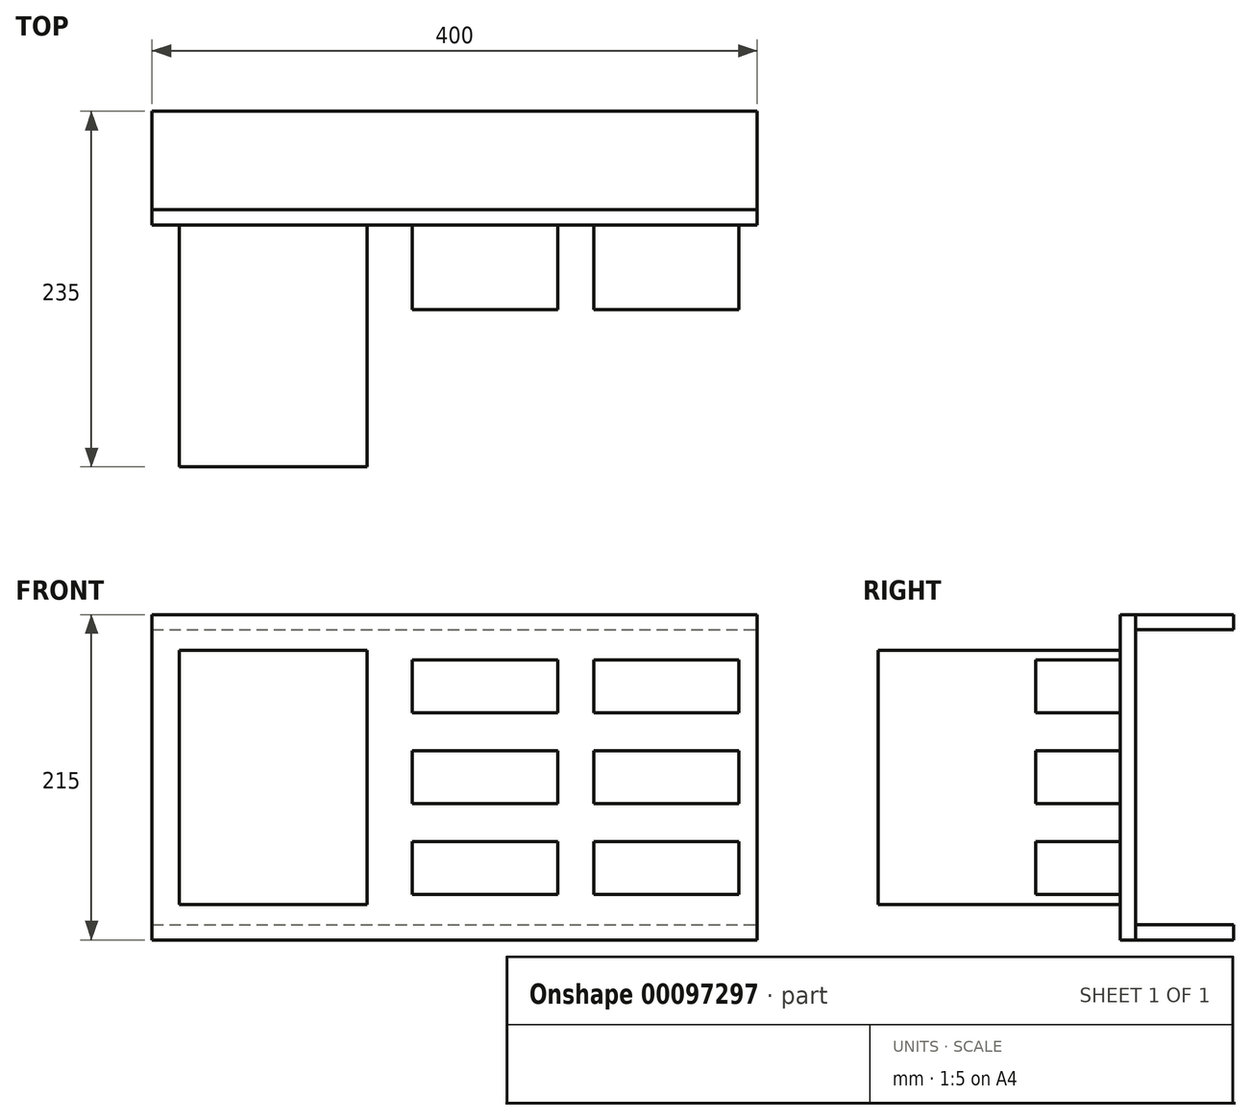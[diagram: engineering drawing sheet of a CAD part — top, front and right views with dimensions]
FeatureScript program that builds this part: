
annotation { "Feature Type Name" : "Feature", "Feature Type Description" : "" }
export const myFeature = defineFeature(function(context is Context, id is Id, definition is map)
    precondition{}
    {
        {
            var Q0;
            Q0=qCreatedBy(makeId("Front.planeOp"),FACE);
            var sketch = newSketch(context, id + "F0", { "sketchPlane" : qUnion([Q0])});
            skLineSegment(sketch, "E0.bottom", {"start": v(-84, -62) * mm, "end": v(84, -62) * mm});
            skLineSegment(sketch, "E0.top", {"start": v(-84, 62) * mm, "end": v(84, 62) * mm});
            skLineSegment(sketch, "E0.left", {"start": v(-84, -62) * mm, "end": v(-84, 62) * mm});
            skLineSegment(sketch, "E0.right", {"start": v(84, -62) * mm, "end": v(84, 62) * mm});
            skPoint(sketch, "E0.middle", {"position": v(0, 0) * mm});
            skLineSegment(sketch, "E1.bottom", {"start": v(-48, -107) * mm, "end": v(48, -107) * mm});
            skLineSegment(sketch, "E1.top", {"start": v(-48, -72) * mm, "end": v(48, -72) * mm});
            skLineSegment(sketch, "E1.left", {"start": v(-48, -107) * mm, "end": v(-48, -72) * mm});
            skLineSegment(sketch, "E1.right", {"start": v(48, -107) * mm, "end": v(48, -72) * mm});
            skPoint(sketch, "E1.middle", {"position": v(0, -89.5) * mm});
            skPoint(sketch, "E1.middle.positionSnap0", {"position": v(0, -62) * mm});
            skPoint(sketch, "E1.centerSnap0", {"position": v(0, -62) * mm});
            skLineSegment(sketch, "E2.bottom", {"start": v(-48, -152) * mm, "end": v(48, -152) * mm});
            skLineSegment(sketch, "E2.top", {"start": v(-48, -117) * mm, "end": v(48, -117) * mm});
            skLineSegment(sketch, "E2.left", {"start": v(-48, -152) * mm, "end": v(-48, -117) * mm});
            skLineSegment(sketch, "E2.right", {"start": v(48, -152) * mm, "end": v(48, -117) * mm});
            skPoint(sketch, "E2.middle", {"position": v(0, -134.5) * mm});
            skLineSegment(sketch, "E3.bottom", {"start": v(-48, -197) * mm, "end": v(48, -197) * mm});
            skLineSegment(sketch, "E3.top", {"start": v(-48, -162) * mm, "end": v(48, -162) * mm});
            skLineSegment(sketch, "E3.left", {"start": v(-48, -197) * mm, "end": v(-48, -162) * mm});
            skLineSegment(sketch, "E3.right", {"start": v(48, -197) * mm, "end": v(48, -162) * mm});
            skPoint(sketch, "E3.middle", {"position": v(0, -179.5) * mm});
            skLineSegment(sketch, "E4.bottom", {"start": v(-48, -242) * mm, "end": v(48, -242) * mm});
            skLineSegment(sketch, "E4.top", {"start": v(-48, -207) * mm, "end": v(48, -207) * mm});
            skLineSegment(sketch, "E4.left", {"start": v(-48, -242) * mm, "end": v(-48, -207) * mm});
            skLineSegment(sketch, "E4.right", {"start": v(48, -242) * mm, "end": v(48, -207) * mm});
            skPoint(sketch, "E4.middle", {"position": v(0, -224.5) * mm});
            skLineSegment(sketch, "E5.bottom", {"start": v(-48, -287) * mm, "end": v(48, -287) * mm});
            skLineSegment(sketch, "E5.top", {"start": v(-48, -252) * mm, "end": v(48, -252) * mm});
            skLineSegment(sketch, "E5.left", {"start": v(-48, -287) * mm, "end": v(-48, -252) * mm});
            skLineSegment(sketch, "E5.right", {"start": v(48, -287) * mm, "end": v(48, -252) * mm});
            skPoint(sketch, "E5.middle", {"position": v(0, -269.5) * mm});
            skLineSegment(sketch, "E6", {"start": v(0, -62) * mm, "end": v(0, -72) * mm, "construction": true});
            skLineSegment(sketch, "E7", {"start": v(0, -107) * mm, "end": v(0, -117) * mm, "construction": true});
            skLineSegment(sketch, "E8", {"start": v(0, -152) * mm, "end": v(0, -162) * mm, "construction": true});
            skLineSegment(sketch, "E9", {"start": v(0, -197) * mm, "end": v(0, -207) * mm, "construction": true});
            skLineSegment(sketch, "E10", {"start": v(0, -242) * mm, "end": v(0, -252) * mm, "construction": true});
            skLineSegment(sketch, "E11.bottom", {"start": v(-52.5, -373.34) * mm, "end": v(52.5, -373.34) * mm});
            skLineSegment(sketch, "E11.top", {"start": v(-52.5, -503.34) * mm, "end": v(52.5, -503.34) * mm});
            skLineSegment(sketch, "E11.left", {"start": v(-52.5, -373.34) * mm, "end": v(-52.5, -503.34) * mm});
            skLineSegment(sketch, "E11.right", {"start": v(52.5, -373.34) * mm, "end": v(52.5, -503.34) * mm});
            skPoint(sketch, "E11.middle", {"position": v(0, -438.34) * mm});
            skLineSegment(sketch, "E12.bottom", {"start": v(-90, 68) * mm, "end": v(90, 68) * mm});
            skLineSegment(sketch, "E12.top", {"start": v(-90, -432) * mm, "end": v(90, -432) * mm});
            skLineSegment(sketch, "E12.left", {"start": v(-90, 68) * mm, "end": v(-90, -432) * mm});
            skLineSegment(sketch, "E12.right", {"start": v(90, 68) * mm, "end": v(90, -432) * mm});
            skPoint(sketch, "E12.middle", {"position": v(0, -182) * mm});
            skSolve(sketch);
        }
        {
            var Q0;
            Q0=qCreatedBy(makeId("Front.planeOp"),FACE);
            var sketch = newSketch(context, id + "F1", { "sketchPlane" : qUnion([Q0])});
            skLineSegment(sketch, "E13.bottom", {"start": v(-200, -107.5) * mm, "end": v(200, -107.5) * mm});
            skLineSegment(sketch, "E13.top", {"start": v(-200, 107.5) * mm, "end": v(200, 107.5) * mm});
            skLineSegment(sketch, "E13.left", {"start": v(-200, -107.5) * mm, "end": v(-200, 107.5) * mm});
            skLineSegment(sketch, "E13.right", {"start": v(200, -107.5) * mm, "end": v(200, 107.5) * mm});
            skPoint(sketch, "E13.middle", {"position": v(0, 0) * mm});
            skLineSegment(sketch, "E14.0", {"start": v(-200, 97.5) * mm, "end": v(200, 97.5) * mm});
            skLineSegment(sketch, "E14.2", {"start": v(-200, -97.5) * mm, "end": v(200, -97.5) * mm});
            skSolve(sketch);
        }
        {
            var Q0;
            Q0 = qSketchRegion(id + "F1", true);
            extrude(context, id + "F2", {"entities" : qUnion([Q0]), "depth" : 10 * mm, "offsetDistance" : 25 * mm});
        }
        {
            var Q0;
            {var subQ0=sQuery(id+"F1.wireOp",EDGE,"E13.top");Q0=makeQuery(id+"F1.imprint","IMPRINT",FACE,{"disambiguationData":[TD([[makeQuery(id+"F1.imprint","IMPRINT",EDGE,{"derivedFrom":subQ0}),-1.0]])]});}
            var Q1;
            {var subQ0=sQuery(id+"F1.wireOp",EDGE,"E13.bottom");Q1=makeQuery(id+"F1.imprint","IMPRINT",FACE,{"disambiguationData":[TD([[makeQuery(id+"F1.imprint","IMPRINT",EDGE,{"derivedFrom":subQ0}),1.0]])]});}
            extrude(context, id + "F3", {"entities" : qUnion([Q0, Q1]), "oppositeDirection" : true, "depth" : 65 * mm, "offsetDistance" : 25 * mm});
        }
        {
            var Q0;
            Q0=makeQuery(id+"F2.opExtrude","CAP_FACE",FACE,{"disambiguationData":[OSD([sQuery(id+"F1.wireOp",EDGE,"E13.bottom"),sQuery(id+"F1.wireOp",EDGE,"E13.top"),sQuery(id+"F1.wireOp",EDGE,"E13.left"),sQuery(id+"F1.wireOp",EDGE,"E13.right")])],"isStart":false});
            var sketch = newSketch(context, id + "F4", { "sketchPlane" : qUnion([Q0])});
            skLineSegment(sketch, "E15.bottom", {"start": v(-182, -84) * mm, "end": v(-58, -84) * mm});
            skLineSegment(sketch, "E15.top", {"start": v(-182, 84) * mm, "end": v(-58, 84) * mm});
            skLineSegment(sketch, "E15.left", {"start": v(-182, -84) * mm, "end": v(-182, 84) * mm});
            skLineSegment(sketch, "E15.right", {"start": v(-58, -84) * mm, "end": v(-58, 84) * mm});
            skPoint(sketch, "E15.middle", {"position": v(-120, 0) * mm});
            skLineSegment(sketch, "E16.bottom", {"start": v(-28, 42.5) * mm, "end": v(68, 42.5) * mm});
            skLineSegment(sketch, "E16.top", {"start": v(-28, 77.5) * mm, "end": v(68, 77.5) * mm});
            skLineSegment(sketch, "E16.left", {"start": v(-28, 42.5) * mm, "end": v(-28, 77.5) * mm});
            skLineSegment(sketch, "E16.right", {"start": v(68, 42.5) * mm, "end": v(68, 77.5) * mm});
            skPoint(sketch, "E16.middle", {"position": v(20, 60) * mm});
            skPoint(sketch, "E17.0.1.0", {"position": v(20, 0) * mm});
            skLineSegment(sketch, "E17.0.1.1", {"start": v(-28, -17.5) * mm, "end": v(-28, 17.5) * mm});
            skLineSegment(sketch, "E17.0.1.2", {"start": v(-28, -17.5) * mm, "end": v(68, -17.5) * mm});
            skLineSegment(sketch, "E17.0.1.3", {"start": v(-28, 17.5) * mm, "end": v(68, 17.5) * mm});
            skLineSegment(sketch, "E17.0.1.4", {"start": v(68, -17.5) * mm, "end": v(68, 17.5) * mm});
            skPoint(sketch, "E17.0.2.0", {"position": v(20, -60) * mm});
            skLineSegment(sketch, "E17.0.2.1", {"start": v(-28, -77.5) * mm, "end": v(-28, -42.5) * mm});
            skLineSegment(sketch, "E17.0.2.2", {"start": v(-28, -77.5) * mm, "end": v(68, -77.5) * mm});
            skLineSegment(sketch, "E17.0.2.3", {"start": v(-28, -42.5) * mm, "end": v(68, -42.5) * mm});
            skLineSegment(sketch, "E17.0.2.4", {"start": v(68, -77.5) * mm, "end": v(68, -42.5) * mm});
            skPoint(sketch, "E17.1.0.0", {"position": v(140, 60) * mm});
            skLineSegment(sketch, "E17.1.0.1", {"start": v(92, 42.5) * mm, "end": v(92, 77.5) * mm});
            skLineSegment(sketch, "E17.1.0.2", {"start": v(92, 42.5) * mm, "end": v(188, 42.5) * mm});
            skLineSegment(sketch, "E17.1.0.3", {"start": v(92, 77.5) * mm, "end": v(188, 77.5) * mm});
            skLineSegment(sketch, "E17.1.0.4", {"start": v(188, 42.5) * mm, "end": v(188, 77.5) * mm});
            skPoint(sketch, "E17.1.1.0", {"position": v(140, 0) * mm});
            skLineSegment(sketch, "E17.1.1.1", {"start": v(92, -17.5) * mm, "end": v(92, 17.5) * mm});
            skLineSegment(sketch, "E17.1.1.2", {"start": v(92, -17.5) * mm, "end": v(188, -17.5) * mm});
            skLineSegment(sketch, "E17.1.1.3", {"start": v(92, 17.5) * mm, "end": v(188, 17.5) * mm});
            skLineSegment(sketch, "E17.1.1.4", {"start": v(188, -17.5) * mm, "end": v(188, 17.5) * mm});
            skPoint(sketch, "E17.1.2.0", {"position": v(140, -60) * mm});
            skLineSegment(sketch, "E17.1.2.1", {"start": v(92, -77.5) * mm, "end": v(92, -42.5) * mm});
            skLineSegment(sketch, "E17.1.2.2", {"start": v(92, -77.5) * mm, "end": v(188, -77.5) * mm});
            skLineSegment(sketch, "E17.1.2.3", {"start": v(92, -42.5) * mm, "end": v(188, -42.5) * mm});
            skLineSegment(sketch, "E17.1.2.4", {"start": v(188, -77.5) * mm, "end": v(188, -42.5) * mm});
            skLineSegment(sketch, "E17.direction1", {"start": v(20, 60) * mm, "end": v(140, 60) * mm, "construction": true});
            skLineSegment(sketch, "E17.direction2", {"start": v(20, 60) * mm, "end": v(20, 0) * mm, "construction": true});
            skSolve(sketch);
        }
        {
            var Q0;
            Q0=makeQuery(id+"F4.imprint","IMPRINT",FACE,{"disambiguationData":[TD([[makeQuery(id+"F4.imprint","IMPRINT",EDGE,{"derivedFrom":sQuery(id+"F4.wireOp",EDGE,"E15.bottom")}),1.0]])]});
            extrude(context, id + "F5", {"entities" : qUnion([Q0]), "depth" : 160 * mm, "offsetDistance" : 25 * mm});
        }
        {
            var Q0;
            Q0=makeQuery(id+"F4.imprint","IMPRINT",FACE,{"disambiguationData":[TD([[makeQuery(id+"F4.imprint","IMPRINT",EDGE,{"derivedFrom":sQuery(id+"F4.wireOp",EDGE,"E16.bottom")}),1.0]])]});
            var Q1;
            Q1=makeQuery(id+"F4.imprint","IMPRINT",FACE,{"disambiguationData":[TD([[makeQuery(id+"F4.imprint","IMPRINT",EDGE,{"derivedFrom":sQuery(id+"F4.wireOp",EDGE,"E17.0.1.1")}),-1.0]])]});
            var Q2;
            Q2=makeQuery(id+"F4.imprint","IMPRINT",FACE,{"disambiguationData":[TD([[makeQuery(id+"F4.imprint","IMPRINT",EDGE,{"derivedFrom":sQuery(id+"F4.wireOp",EDGE,"E17.0.2.1")}),-1.0]])]});
            var Q3;
            Q3=makeQuery(id+"F4.imprint","IMPRINT",FACE,{"disambiguationData":[TD([[makeQuery(id+"F4.imprint","IMPRINT",EDGE,{"derivedFrom":sQuery(id+"F4.wireOp",EDGE,"E17.1.0.1")}),-1.0]])]});
            var Q4;
            Q4=makeQuery(id+"F4.imprint","IMPRINT",FACE,{"disambiguationData":[TD([[makeQuery(id+"F4.imprint","IMPRINT",EDGE,{"derivedFrom":sQuery(id+"F4.wireOp",EDGE,"E17.1.1.1")}),-1.0]])]});
            var Q5;
            Q5=makeQuery(id+"F4.imprint","IMPRINT",FACE,{"disambiguationData":[TD([[makeQuery(id+"F4.imprint","IMPRINT",EDGE,{"derivedFrom":sQuery(id+"F4.wireOp",EDGE,"E17.1.2.1")}),-1.0]])]});
            extrude(context, id + "F6", {"entities" : qUnion([Q0, Q1, Q2, Q3, Q4, Q5]), "depth" : 56 * mm, "offsetDistance" : 25 * mm});
        }
    });
